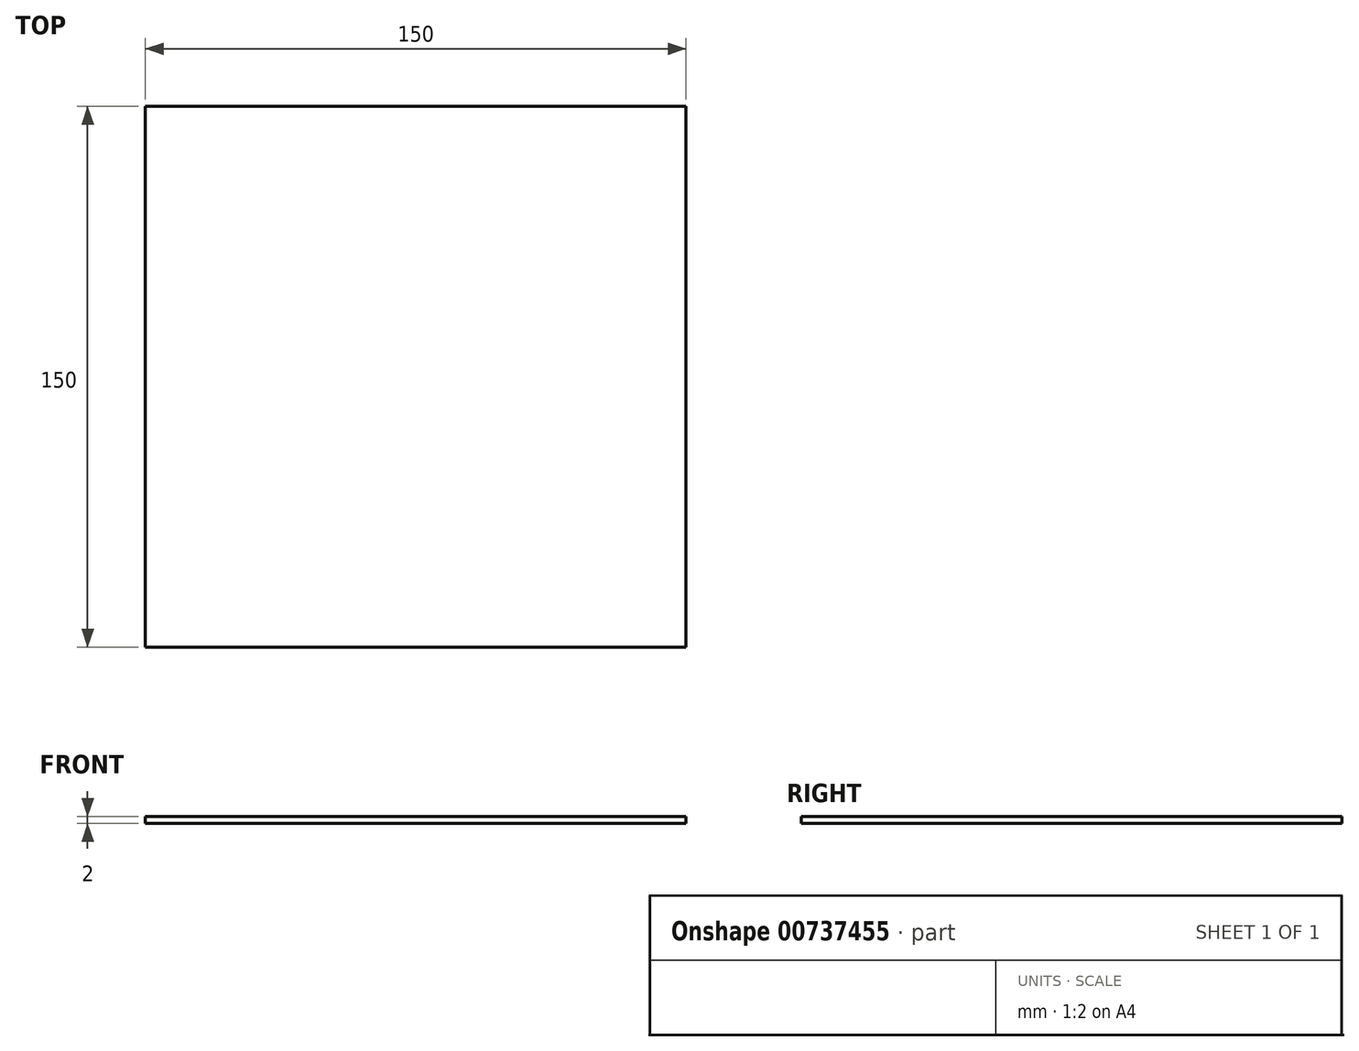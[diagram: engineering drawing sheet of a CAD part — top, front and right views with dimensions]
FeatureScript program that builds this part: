
annotation { "Feature Type Name" : "Feature", "Feature Type Description" : "" }
export const myFeature = defineFeature(function(context is Context, id is Id, definition is map)
    precondition{}
    {
        {
            var Q0;
            Q0=qCreatedBy(makeId("Top.planeOp"),FACE);
            var sketch = newSketch(context, id + "F0", { "sketchPlane" : qUnion([Q0])});
            skLineSegment(sketch, "E0.bottom", {"start": v(75, -75) * mm, "end": v(-75, -75) * mm});
            skLineSegment(sketch, "E0.top", {"start": v(75, 75) * mm, "end": v(-75, 75) * mm});
            skLineSegment(sketch, "E0.left", {"start": v(75, -75) * mm, "end": v(75, 75) * mm});
            skLineSegment(sketch, "E0.right", {"start": v(-75, -75) * mm, "end": v(-75, 75) * mm});
            skPoint(sketch, "E0.middle", {"position": v(0, 0) * mm});
            skSolve(sketch);
        }
        {
            var Q0;
            Q0=makeQuery(id+"F0.imprint","IMPRINT",FACE,{"disambiguationData":[TD([[makeQuery(id+"F0.imprint","IMPRINT",EDGE,{"derivedFrom":sQuery(id+"F0.wireOp",EDGE,"E0.bottom")}),-1.0]])]});
            extrude(context, id + "F1", {"entities" : qUnion([Q0]), "depth" : 2 * mm, "offsetDistance" : 25 * mm});
        }
        {
            var Q0;
            Q0=makeQuery(id+"F5LlTyRMBxMwHFN_1.boolean.opBoolean","MERGE",FACE,{"derivedFrom":[makeQuery(id+"F1.opExtrude","SWEPT_FACE",FACE,{"disambiguationData":[OSD([sQuery(id+"F0.wireOp",EDGE,"E0.top")])]}),makeQuery(id+"F5LlTyRMBxMwHFN_1.opExtrude","SWEPT_FACE",FACE,{"disambiguationData":[OSD([sQuery(id+"FUkvjcnhKxgeXgy_1.wireOp",EDGE,"zehdIvbX-nbih-Wtls-b9Qk-RFu4nM5vhBie")])]})]});
            var sketch = newSketch(context, id + "F2", { "sketchPlane" : qUnion([Q0])});
            skCircle(sketch, "E1", {"center": v(-2.38, 4.93) * mm, "radius": 1 * mm});
            skSolve(sketch);
        }
        {
            var Q0;
            Q0=sQuery(id+"F2.wireOp",VERTEX,"E1.center");
            var Q1;
            Q1=makeQuery(id+"F1.opExtrude","SWEPT_BODY",BODY,{"disambiguationData":[OSD([sQuery(id+"F0.wireOp",EDGE,"E0.bottom"),sQuery(id+"F0.wireOp",EDGE,"E0.top"),sQuery(id+"F0.wireOp",EDGE,"E0.left"),sQuery(id+"F0.wireOp",EDGE,"E0.right")])]});
            hole(context, id + "F3", {"style" : HoleStyle.SIMPLE, "endStyle" : HoleEndStyle.THROUGH, "holeDiameter" : 2 * mm, "majorDiameter" : 5 * mm, "isTappedThrough" : true, "tappedDepth" : 12 * mm, "tapClearance" : 3, "locations" : qUnion([Q0]), "scope" : qUnion([Q1])});
        }
    });
